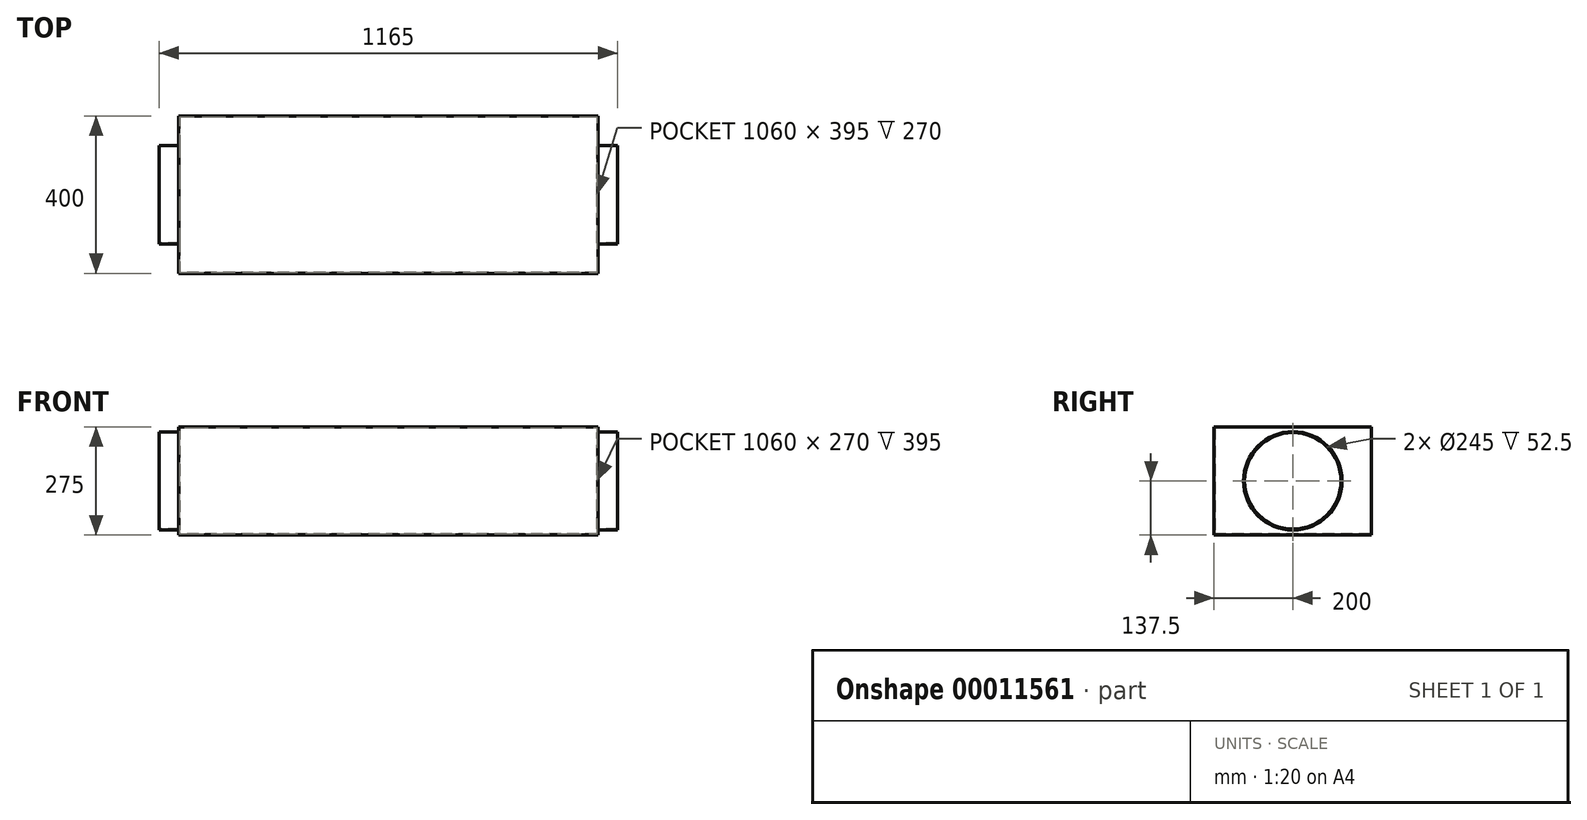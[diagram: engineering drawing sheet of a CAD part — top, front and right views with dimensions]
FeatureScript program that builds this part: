
annotation { "Feature Type Name" : "Feature", "Feature Type Description" : "" }
export const myFeature = defineFeature(function(context is Context, id is Id, definition is map)
    precondition{}
    {
        {
            var Q0;
            Q0=qCreatedBy(makeId("Right.planeOp"),FACE);
            var sketch = newSketch(context, id + "F0", { "sketchPlane" : qUnion([Q0])});
            skLineSegment(sketch, "E0.rect.bottom", {"start": v(200, 137.5) * mm, "end": v(-200, 137.5) * mm});
            skLineSegment(sketch, "E0.rect.top", {"start": v(200, -137.5) * mm, "end": v(-200, -137.5) * mm});
            skLineSegment(sketch, "E0.rect.left", {"start": v(200, 137.5) * mm, "end": v(200, -137.5) * mm});
            skLineSegment(sketch, "E0.rect.right", {"start": v(-200, 137.5) * mm, "end": v(-200, -137.5) * mm});
            skPoint(sketch, "E0.rect.middle", {"position": v(0, 0) * mm});
            skSolve(sketch);
        }
        {
            var Q0;
            Q0=qSketchRegion(id+"F0",true);
            extrude(context, id + "F1", {"entities" : qUnion([Q0]), "endBound" : BoundingType.SYMMETRIC, "depth" : 1065 * mm});
        }
        {
            var Q0;
            Q0=qCreatedBy(makeId("Right.planeOp"),FACE);
            var sketch = newSketch(context, id + "F2", { "sketchPlane" : qUnion([Q0])});
            skCircle(sketch, "E1", {"center": v(0, 0) * mm, "radius": 125 * mm});
            skSolve(sketch);
        }
        {
            var Q0;
            Q0=qSketchRegion(id+"F2",true);
            extrude(context, id + "F3", {"entities" : qUnion([Q0]), "operationType" : NewBodyOperationType.ADD, "endBound" : BoundingType.SYMMETRIC, "depth" : 1165 * mm});
        }
        {
            var Q0;
            Q0=makeQuery(id+"F3.opExtrude","CAP_FACE",FACE,{"disambiguationData":[OSD([sQuery(id+"F2.wireOp",EDGE,"E1")])],"isStart":false});
            var Q1;
            Q1=makeQuery(id+"F3.opExtrude","CAP_FACE",FACE,{"disambiguationData":[OSD([sQuery(id+"F2.wireOp",EDGE,"E1")])],"isStart":true});
            shell(context, id + "F4", {"entities" : qUnion([Q0, Q1]), "thickness" : 2.5 * mm});
        }
    });
